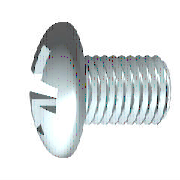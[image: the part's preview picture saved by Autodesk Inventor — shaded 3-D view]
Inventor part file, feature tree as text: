
AUTODESK INVENTOR PART (.ipt)
format: ipt  version: 2022 (Build 260153000, 153)  size: 279,040 bytes
history: native  units: mm (DEFAULTED — no unit token found)
features: other x2, plane x2, extrude x1
ambient origin geometry x7: Origin, YZ Plane, XZ Plane, X Axis, Y Axis, Z Axis, Center Point
bodies: Solid1 (feature_tree)
feature tree (5):
  other  "Базовый элемент"
  plane  "Work Plane1"
  extrude  "Паз"  Depth=4.0mm
  other  "Вырез"
  plane  "Work Plane3"
